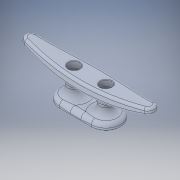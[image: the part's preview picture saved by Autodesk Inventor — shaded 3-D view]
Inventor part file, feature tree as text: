
AUTODESK INVENTOR PART (.ipt)
format: ipt  version: 2018 (Build 220112000, 112)  size: 916,480 bytes
history: native  units: in
note: dims shown in document units (in); Inventor stores cm internally (conversion verified against a paired STEP export)
features: mirror x1
ambient origin geometry x8: Origin, YZ Plane, XZ Plane, XY Plane, X Axis, Y Axis, Z Axis, Center Point
bodies: Solid1 (feature_tree)
feature tree (1):
  mirror  "Mirror2"
